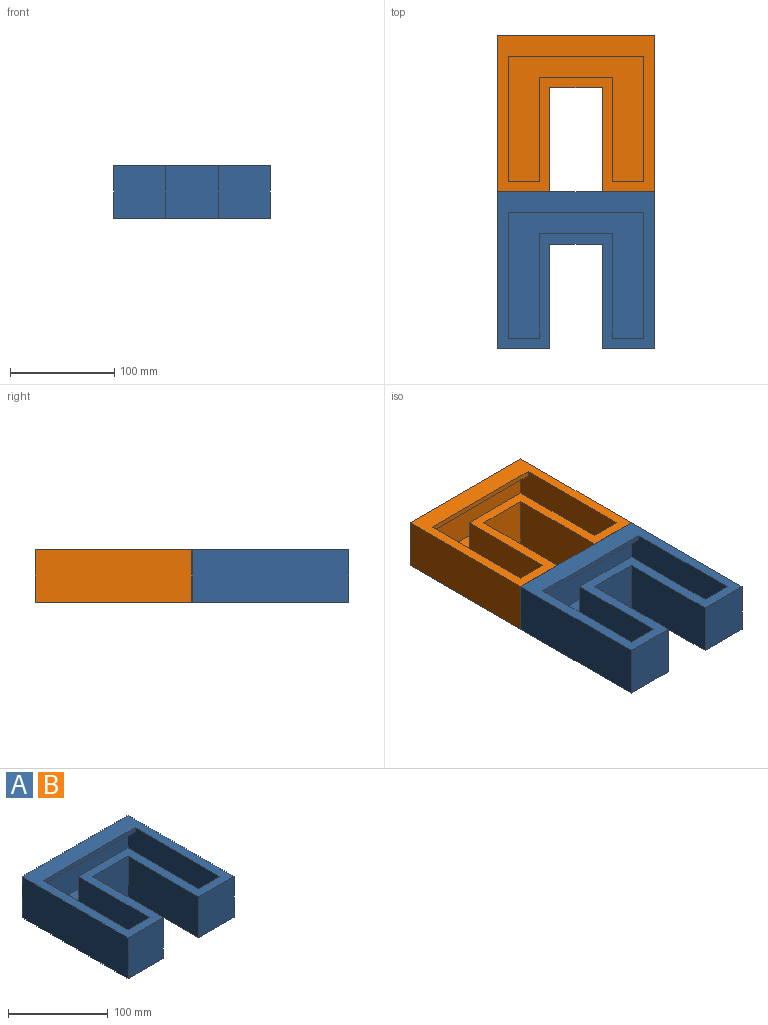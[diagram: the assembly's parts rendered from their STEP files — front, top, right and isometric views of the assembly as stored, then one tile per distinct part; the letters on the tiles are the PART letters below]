
ASSEMBLY  parts=2 mates=1
PART A: 21 faces, bbox 150x150x50 mm
  f0: plane 130x40mm, normal (0,-1,0), area 5200mm2, adj f1,f10,f18,f19
  f1: plane 130x45mm, normal (-1,0,0), area 5800mm2, adj f0,f11,f17,f18,f19,f20
  f2: plane 150x150mm, normal (0,0,-1), area 17500mm2, adj f3,f4,f5,f6,f7,f8,f9,f16
  f3: plane 150x50mm, normal (-1,0,0), area 7500mm2, adj f2,f4,f16,f17
  f4: plane 50x50mm, normal (0,-1,0), area 2500mm2, adj f2,f3,f5,f17
  f5: plane 100x50mm, normal (1,0,0), area 5000mm2, adj f2,f4,f6,f17
  f6: plane 50x50mm, normal (0,-1,0), area 2500mm2, adj f2,f5,f7,f17
  f7: plane 100x50mm, normal (-1,0,0), area 5000mm2, adj f2,f6,f8,f17
  f8: plane 50x50mm, normal (0,-1,0), area 2500mm2, adj f2,f7,f9,f17
  f9: plane 150x50mm, normal (1,0,0), area 7500mm2, adj f2,f8,f16,f17
  f10: plane 130x45mm, normal (1,0,0), area 5800mm2, adj f0,f15,f17,f18,f19,f20
  f11: plane 45x30mm, normal (0,1,0), area 1350mm2, adj f1,f12,f17,f18
  f12: plane 100x45mm, normal (1,0,0), area 4500mm2, adj f11,f13,f17,f18
  f13: plane 70x45mm, normal (0,1,0), area 3150mm2, adj f12,f14,f17,f18
  f14: plane 100x45mm, normal (-1,0,0), area 4500mm2, adj f13,f15,f17,f18
  f15: plane 45x30mm, normal (0,1,0), area 1350mm2, adj f10,f14,f17,f18
  f16: plane 150x50mm, normal (0,1,0), area 7500mm2, adj f2,f3,f9,f17
  f17: plane 150x150mm, normal (0,0,1), area 8900mm2, adj f1,f3,f4,f5,f6,f7,f8,f9
  f18: plane 130x130mm, normal (0,0,1), area 9900mm2, adj f0,f1,f10,f11,f12,f13,f14,f15
  f19: plane 130x10mm, normal (0,0,-1), area 1300mm2, adj f0,f1,f10,f20
  f20: plane 130x5mm, normal (0,-1,0), area 650mm2, adj f1,f10,f17,f19
PART B: same geometry as A
PLACE A t=(-3.41,-97.05,9.83)mm
PLACE B t=(-3.41,52.95,9.83)mm
MATE fastened B.f8 <-> A.f16  axis (0,-1,0) through (-28.41,52.95,34.83)mm
